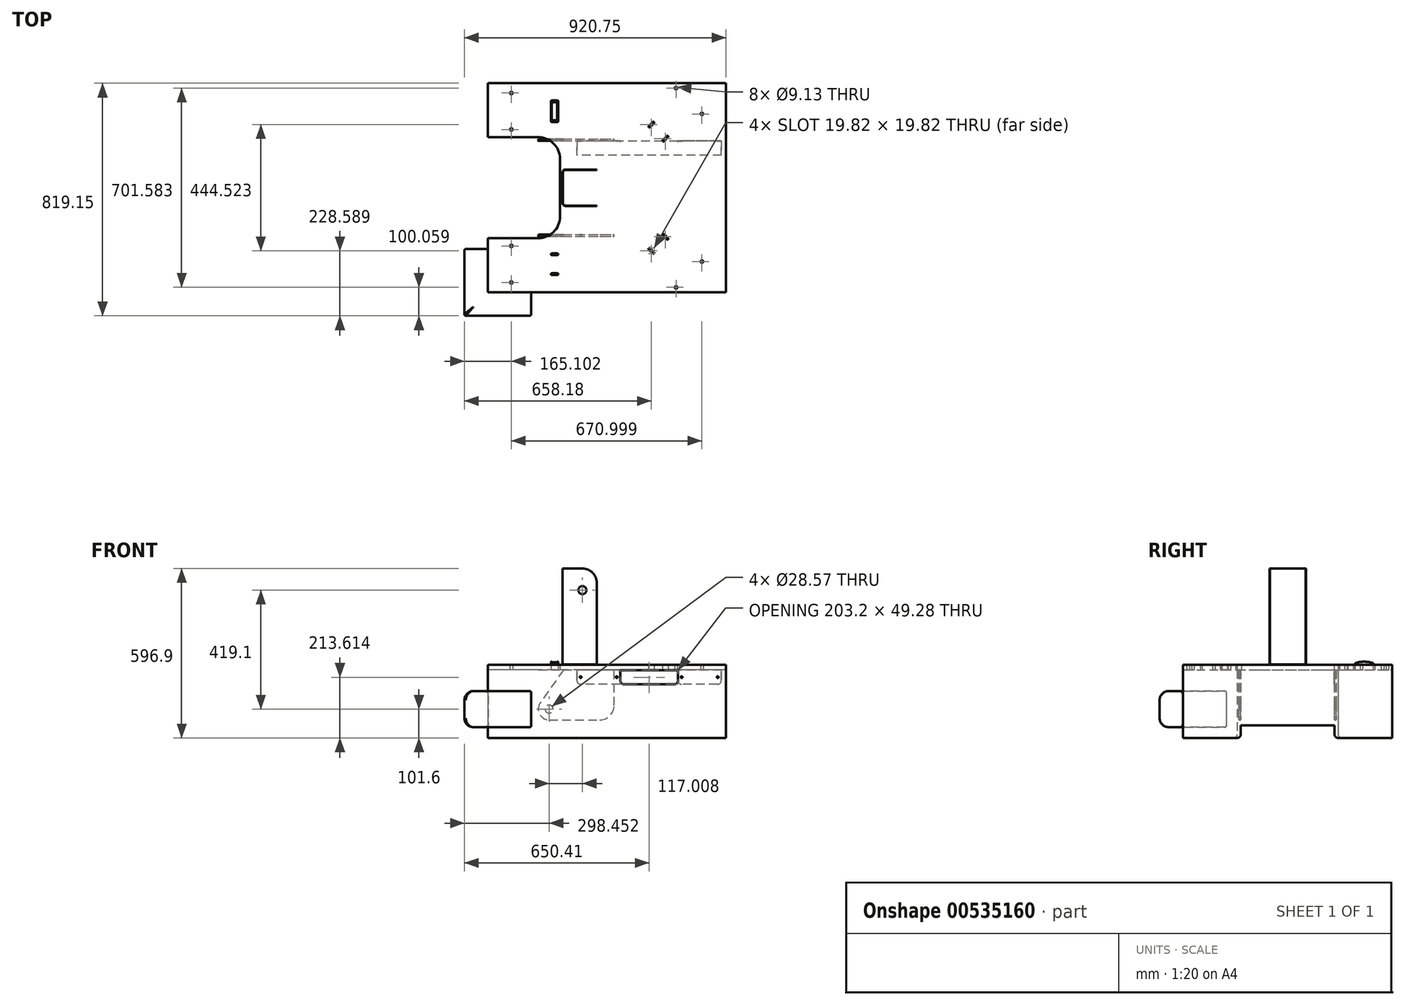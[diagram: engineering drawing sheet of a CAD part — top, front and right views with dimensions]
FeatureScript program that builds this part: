
annotation { "Feature Type Name" : "Feature", "Feature Type Description" : "" }
export const myFeature = defineFeature(function(context is Context, id is Id, definition is map)
    precondition{}
    {
        {
            var Q0;
            Q0=qCreatedBy(makeId("Top.planeOp"),FACE);
            var sketch = newSketch(context, id + "F0", { "sketchPlane" : qUnion([Q0])});
            skLineSegment(sketch, "E0.bottom", {"start": v(-491.66, 457.2) * mm, "end": v(524.34, 457.2) * mm});
            skLineSegment(sketch, "E0.top", {"start": v(-491.66, -457.2) * mm, "end": v(524.34, -457.2) * mm});
            skLineSegment(sketch, "E0.left", {"start": v(-491.66, 457.2) * mm, "end": v(-491.66, -457.2) * mm});
            skLineSegment(sketch, "E0.right", {"start": v(524.34, 457.2) * mm, "end": v(524.34, -457.2) * mm});
            skLineSegment(sketch, "E1.bottom", {"start": v(-301.16, -193.2) * mm, "end": v(-237.66, -193.2) * mm});
            skLineSegment(sketch, "E1.top", {"start": v(-301.16, -345.6) * mm, "end": v(-237.66, -345.6) * mm});
            skLineSegment(sketch, "E1.left", {"start": v(-301.16, -193.2) * mm, "end": v(-301.16, -345.6) * mm});
            skLineSegment(sketch, "E1.right", {"start": v(-237.66, -193.2) * mm, "end": v(-237.66, -345.6) * mm});
            skLineSegment(sketch, "E2.bottom", {"start": v(-301.16, 345.6) * mm, "end": v(-237.66, 345.6) * mm});
            skLineSegment(sketch, "E2.top", {"start": v(-301.16, 193.2) * mm, "end": v(-237.66, 193.2) * mm});
            skLineSegment(sketch, "E2.left", {"start": v(-301.16, 345.6) * mm, "end": v(-301.16, 193.2) * mm});
            skLineSegment(sketch, "E2.right", {"start": v(-237.66, 345.6) * mm, "end": v(-237.66, 193.2) * mm});
            skLineSegment(sketch, "E3", {"start": v(-301.16, -345.6) * mm, "end": v(-237.66, -193.2) * mm, "construction": true});
            skLineSegment(sketch, "E4", {"start": v(-269.4, -269.4) * mm, "end": v(0, 0) * mm, "construction": true});
            skLineSegment(sketch, "E5", {"start": v(-301.16, 345.6) * mm, "end": v(-237.66, 193.2) * mm, "construction": true});
            skLineSegment(sketch, "E6", {"start": v(-269.4, 269.4) * mm, "end": v(0, 0) * mm, "construction": true});
            skLineSegment(sketch, "E7", {"start": v(435.44, -368.3) * mm, "end": v(-402.76, -368.3) * mm, "construction": true});
            skLineSegment(sketch, "E8", {"start": v(-402.76, -368.3) * mm, "end": v(-402.76, 368.3) * mm, "construction": true});
            skLineSegment(sketch, "E9", {"start": v(-402.76, 368.3) * mm, "end": v(435.44, 368.3) * mm, "construction": true});
            skLineSegment(sketch, "E10.bottom", {"start": v(224.5, 332.27) * mm, "end": v(332.27, 224.5) * mm});
            skLineSegment(sketch, "E10.top", {"start": v(206.55, 314.3) * mm, "end": v(314.3, 206.55) * mm});
            skLineSegment(sketch, "E10.left", {"start": v(224.5, 332.27) * mm, "end": v(206.55, 314.3) * mm});
            skLineSegment(sketch, "E10.right", {"start": v(332.27, 224.5) * mm, "end": v(314.3, 206.55) * mm});
            skPoint(sketch, "E10.middle", {"position": v(269.4, 269.4) * mm});
            skLineSegment(sketch, "E11", {"start": v(0, 0) * mm, "end": v(269.4, 269.4) * mm, "construction": true});
            skLineSegment(sketch, "E12.bottom", {"start": v(314.3, -206.55) * mm, "end": v(206.55, -314.3) * mm});
            skLineSegment(sketch, "E12.top", {"start": v(332.27, -224.5) * mm, "end": v(224.5, -332.27) * mm});
            skLineSegment(sketch, "E12.left", {"start": v(314.3, -206.55) * mm, "end": v(332.27, -224.5) * mm});
            skLineSegment(sketch, "E12.right", {"start": v(206.55, -314.3) * mm, "end": v(224.5, -332.27) * mm});
            skPoint(sketch, "E12.middle", {"position": v(269.4, -269.4) * mm});
            skLineSegment(sketch, "E13", {"start": v(0, 0) * mm, "end": v(269.4, -269.4) * mm, "construction": true});
            skLineSegment(sketch, "E14", {"start": v(-402.76, 215.9) * mm, "end": v(-485.3, 215.9) * mm, "construction": true});
            skLineSegment(sketch, "E15", {"start": v(-485.3, 215.9) * mm, "end": v(-485.3, 450.85) * mm, "construction": true});
            skLineSegment(sketch, "E16", {"start": v(-485.3, 450.85) * mm, "end": v(518, 450.85) * mm, "construction": true});
            skLineSegment(sketch, "E17", {"start": v(-402.76, -215.9) * mm, "end": v(-485.3, -215.9) * mm, "construction": true});
            skLineSegment(sketch, "E18", {"start": v(-485.3, -215.9) * mm, "end": v(-485.3, -450.85) * mm, "construction": true});
            skLineSegment(sketch, "E19", {"start": v(-485.3, -450.85) * mm, "end": v(518, -450.85) * mm, "construction": true});
            skCircle(sketch, "E20", {"center": v(-345.42, 0) * mm, "radius": 139.7 * mm, "construction": true});
            skLineSegment(sketch, "E21.bottom", {"start": v(-398.8, 177.8) * mm, "end": v(-170.2, 177.8) * mm, "construction": true});
            skLineSegment(sketch, "E21.top", {"start": v(-398.8, -177.8) * mm, "end": v(-170.2, -177.8) * mm, "construction": true});
            skLineSegment(sketch, "E21.left", {"start": v(-398.8, 177.8) * mm, "end": v(-398.8, -177.8) * mm, "construction": true});
            skLineSegment(sketch, "E21.right", {"start": v(-170.2, 177.8) * mm, "end": v(-170.2, -177.8) * mm, "construction": true});
            skPoint(sketch, "E21.middle", {"position": v(-284.5, 0) * mm});
            skLineSegment(sketch, "E22", {"start": v(-269.4, 269.4) * mm, "end": v(-269.4, 383.7) * mm, "construction": true});
            skLineSegment(sketch, "E23", {"start": v(251.45, 305.33) * mm, "end": v(278.39, 332.27) * mm, "construction": true});
            skLineSegment(sketch, "E24", {"start": v(278.39, 332.27) * mm, "end": v(332.27, 278.39) * mm, "construction": true});
            skLineSegment(sketch, "E25", {"start": v(332.27, 278.39) * mm, "end": v(305.33, 251.45) * mm, "construction": true});
            skPoint(sketch, "E26.startSnap0", {"position": v(260.43, 260.43) * mm});
            skPoint(sketch, "E27", {"position": v(-170.2, 0) * mm});
            skLineSegment(sketch, "E28", {"start": v(435.44, -368.3) * mm, "end": v(435.44, 368.3) * mm, "construction": true});
            skLineSegment(sketch, "E29", {"start": v(518, 450.85) * mm, "end": v(518, -450.85) * mm, "construction": true});
            skSolve(sketch);
        }
        {
            var Q0;
            Q0=qCreatedBy(makeId("Front.planeOp"),FACE);
            var sketch = newSketch(context, id + "F1", { "sketchPlane" : qUnion([Q0])});
            skLineSegment(sketch, "E30.bottom", {"start": v(-491.66, 50.8) * mm, "end": v(-212.26, 50.8) * mm});
            skLineSegment(sketch, "E30.top", {"start": v(-491.66, 0) * mm, "end": v(-212.26, 0) * mm});
            skLineSegment(sketch, "E30.left", {"start": v(-491.66, 50.8) * mm, "end": v(-491.66, 0) * mm});
            skLineSegment(sketch, "E30.right", {"start": v(-212.26, 50.8) * mm, "end": v(-212.26, 0) * mm});
            skCircle(sketch, "E31", {"center": v(-186.86, 114.3) * mm, "radius": 15.32 * mm});
            skLineSegment(sketch, "E32.bottom", {"start": v(-250.36, 139.7) * mm, "end": v(-301.16, 139.7) * mm});
            skLineSegment(sketch, "E32.top", {"start": v(-250.36, 419.1) * mm, "end": v(-301.16, 419.1) * mm});
            skLineSegment(sketch, "E32.left", {"start": v(-250.36, 139.7) * mm, "end": v(-250.36, 419.1) * mm});
            skLineSegment(sketch, "E32.right", {"start": v(-301.16, 139.7) * mm, "end": v(-301.16, 419.1) * mm});
            skLineSegment(sketch, "E33", {"start": v(-491.66, 330.2) * mm, "end": v(-224.96, 330.2) * mm});
            skLineSegment(sketch, "E34", {"start": v(-224.96, 330.2) * mm, "end": v(-263.06, 365.13) * mm});
            skLineSegment(sketch, "E35", {"start": v(-263.06, 365.13) * mm, "end": v(-263.06, 352.43) * mm});
            skLineSegment(sketch, "E36", {"start": v(-263.06, 352.43) * mm, "end": v(-491.66, 352.43) * mm});
            skLineSegment(sketch, "E37", {"start": v(-491.66, 352.43) * mm, "end": v(-491.66, 330.2) * mm});
            skLineSegment(sketch, "E38", {"start": v(-301.16, 364.5) * mm, "end": v(-250.36, 364.5) * mm});
            skArc(sketch, "E39", {"start": v(-186.86, 0) * mm, "mid": v(-106.04, 33.48) * mm, "end": v(-72.56, 114.3) * mm});
            skSolve(sketch);
        }
        {
            var Q0;
            Q0=qCreatedBy(makeId("Top.planeOp"),FACE);
            var sketch = newSketch(context, id + "F2", { "sketchPlane" : qUnion([Q0])});
            skLineSegment(sketch, "E40.0", {"start": v(-402.76, 368.3) * mm, "end": v(435.44, 368.3) * mm});
            skArc(sketch, "E41.0", {"start": v(117.94, -368.3) * mm, "mid": v(486.24, 0) * mm, "end": v(117.94, 368.3) * mm, "construction": true});
            skLineSegment(sketch, "E42.0", {"start": v(435.44, -368.3) * mm, "end": v(-402.76, -368.3) * mm});
            skLineSegment(sketch, "E43.0", {"start": v(-402.76, -368.3) * mm, "end": v(-402.76, 368.3) * mm});
            skLineSegment(sketch, "E44.0", {"start": v(117.94, 368.3) * mm, "end": v(245.94, 368.3) * mm, "construction": true});
            skArc(sketch, "E45.0", {"start": v(283.93, 367.12) * mm, "mid": v(264.94, 368) * mm, "end": v(245.94, 368.3) * mm, "construction": true});
            skArc(sketch, "E46.0", {"start": v(283.93, 367.12) * mm, "mid": v(323.68, 354.89) * mm, "end": v(353.52, 325.92) * mm, "construction": true});
            skArc(sketch, "E47.0", {"start": v(353.52, 325.92) * mm, "mid": v(447.96, 0) * mm, "end": v(353.52, -325.92) * mm, "construction": true});
            skArc(sketch, "E48.0", {"start": v(353.52, -325.92) * mm, "mid": v(323.68, -354.89) * mm, "end": v(283.93, -367.12) * mm, "construction": true});
            skArc(sketch, "E49.0", {"start": v(283.93, -367.12) * mm, "mid": v(264.94, -368) * mm, "end": v(245.94, -368.3) * mm, "construction": true});
            skLineSegment(sketch, "E50.0", {"start": v(117.94, -368.3) * mm, "end": v(245.94, -368.3) * mm, "construction": true});
            skLineSegment(sketch, "E51.0", {"start": v(435.44, -368.3) * mm, "end": v(435.44, 368.3) * mm});
            skSolve(sketch);
        }
        {
            var Q0;
            Q0=qSketchRegion(id+"F2",true);
            extrude(context, id + "F3", {"entities" : qUnion([Q0]), "depth" : 254 * mm, "hasSecondDirection" : true, "secondDirectionOppositeDirection" : true, "secondDirectionDepth" : -12.7 * mm});
        }
        {
            var Q0;
            Q0=makeQuery(id+"F3.opExtrude","CAP_FACE",FACE,{"disambiguationData":[OSD([sQuery(id+"F2.wireOp",EDGE,"E40.0"),sQuery(id+"F2.wireOp",EDGE,"E41.0"),sQuery(id+"F2.wireOp",EDGE,"E42.0"),sQuery(id+"F2.wireOp",EDGE,"E43.0")])],"isStart":true});
            shell(context, id + "F4", {"entities" : qUnion([Q0]), "thickness" : 1.52 * mm});
        }
        {
            var Q0;
            Q0=qCreatedBy(makeId("Top.planeOp"),FACE);
            var sketch = newSketch(context, id + "F5", { "sketchPlane" : qUnion([Q0])});
            skLineSegment(sketch, "E52.bottom", {"start": v(-402.76, 177.8) * mm, "end": v(-148.76, 177.8) * mm});
            skLineSegment(sketch, "E52.top", {"start": v(-402.76, -177.8) * mm, "end": v(-148.76, -177.8) * mm});
            skLineSegment(sketch, "E52.left", {"start": v(-402.76, 177.8) * mm, "end": v(-402.76, -177.8) * mm});
            skLineSegment(sketch, "E52.right", {"start": v(-148.76, 177.8) * mm, "end": v(-148.76, -177.8) * mm});
            skSolve(sketch);
        }
        {
            var Q0;
            Q0=qSketchRegion(id+"F5",true);
            extrude(context, id + "F6", {"entities" : qUnion([Q0]), "operationType" : NewBodyOperationType.REMOVE, "endBound" : BoundingType.THROUGH_ALL, "depth" : 25.4 * mm});
        }
        {
            var Q0;
            Q0=makeQuery(id+"F6.boolean.opBoolean","COPY",EDGE,{"derivedFrom":makeQuery(id+"F6.opExtrude","SWEPT_EDGE",EDGE,{"disambiguationData":[OSD([sQuery(id+"F5.wireOp",EDGE,"E52.bottom"),sQuery(id+"F5.wireOp",EDGE,"E52.right")])]})});
            var Q1;
            Q1=makeQuery(id+"F6.boolean.opBoolean","COPY",EDGE,{"derivedFrom":makeQuery(id+"F6.opExtrude","SWEPT_EDGE",EDGE,{"disambiguationData":[OSD([sQuery(id+"F5.wireOp",EDGE,"E52.top"),sQuery(id+"F5.wireOp",EDGE,"E52.right")])]})});
            fillet(context, id + "F7", {"entities" : qUnion([Q0, Q1]), "radius" : 76.2 * mm, "tangentPropagation" : true, "allowEdgeOverflow" : false});
        }
        {
            var Q0;
            Q0=makeQuery(id+"F6.boolean.opBoolean","INTERSECT",EDGE,{"derivedFrom":[makeQuery(id+"F3.opExtrude","CAP_FACE",FACE,{"disambiguationData":[OSD([sQuery(id+"F2.wireOp",EDGE,"E40.0"),sQuery(id+"F2.wireOp",EDGE,"E41.0"),sQuery(id+"F2.wireOp",EDGE,"E42.0"),sQuery(id+"F2.wireOp",EDGE,"E43.0")])],"isStart":true}),makeQuery(id+"F6.opExtrude","SWEPT_FACE",FACE,{"disambiguationData":[OSD([sQuery(id+"F5.wireOp",EDGE,"E52.bottom")])]})]});
            var Q1;
            Q1=makeQuery(id+"F6.boolean.opBoolean","INTERSECT",EDGE,{"derivedFrom":[makeQuery(id+"F3.opExtrude","CAP_FACE",FACE,{"disambiguationData":[OSD([sQuery(id+"F2.wireOp",EDGE,"E40.0"),sQuery(id+"F2.wireOp",EDGE,"E41.0"),sQuery(id+"F2.wireOp",EDGE,"E42.0"),sQuery(id+"F2.wireOp",EDGE,"E43.0")])],"isStart":true}),makeQuery(id+"F6.opExtrude","SWEPT_FACE",FACE,{"disambiguationData":[OSD([sQuery(id+"F5.wireOp",EDGE,"E52.top")])]})]});
            fillet(context, id + "F8", {"entities" : qUnion([Q0, Q1]), "radius" : 12.7 * mm, "tangentPropagation" : true, "allowEdgeOverflow" : false});
        }
        {
            var Q0;
            Q0=qCreatedBy(makeId("Top.planeOp"),FACE);
            var sketch = newSketch(context, id + "F9", { "sketchPlane" : qUnion([Q0])});
            skLineSegment(sketch, "E53.0", {"start": v(-402.76, 215.9) * mm, "end": v(-485.3, 215.9) * mm});
            skLineSegment(sketch, "E54.0", {"start": v(-485.3, 215.9) * mm, "end": v(-485.3, 450.85) * mm});
            skLineSegment(sketch, "E55.0", {"start": v(-485.3, 450.85) * mm, "end": v(518, 450.85) * mm});
            skLineSegment(sketch, "E56.0", {"start": v(-485.3, -450.85) * mm, "end": v(518, -450.85) * mm});
            skLineSegment(sketch, "E57.0", {"start": v(-485.3, -215.9) * mm, "end": v(-485.3, -450.85) * mm});
            skLineSegment(sketch, "E58.0", {"start": v(-402.76, -215.9) * mm, "end": v(-485.3, -215.9) * mm});
            skLineSegment(sketch, "E59.0", {"start": v(435.44, -368.3) * mm, "end": v(-402.76, -368.3) * mm});
            skLineSegment(sketch, "E60.0", {"start": v(-402.76, 368.3) * mm, "end": v(435.44, 368.3) * mm});
            skLineSegment(sketch, "E61.0", {"start": v(-402.76, -368.3) * mm, "end": v(-402.76, 368.3) * mm});
            skLineSegment(sketch, "E62", {"start": v(-402.76, 215.9) * mm, "end": v(-402.76, 368.3) * mm});
            skLineSegment(sketch, "E63", {"start": v(-402.76, -215.9) * mm, "end": v(-402.76, -368.3) * mm});
            skLineSegment(sketch, "E64.0", {"start": v(518, 450.85) * mm, "end": v(518, -450.85) * mm});
            skLineSegment(sketch, "E65", {"start": v(-250.36, 368.3) * mm, "end": v(-250.36, 450.85) * mm});
            skLineSegment(sketch, "E66", {"start": v(-250.36, -368.3) * mm, "end": v(-250.36, -450.85) * mm});
            skLineSegment(sketch, "E67", {"start": v(283.04, 450.85) * mm, "end": v(283.04, 368.3) * mm});
            skLineSegment(sketch, "E68", {"start": v(283.04, -368.3) * mm, "end": v(283.04, -450.85) * mm});
            skLineSegment(sketch, "E69", {"start": v(518, 215.9) * mm, "end": v(435.44, 215.9) * mm});
            skLineSegment(sketch, "E70.0", {"start": v(435.44, -368.3) * mm, "end": v(435.44, 368.3) * mm});
            skLineSegment(sketch, "E71", {"start": v(435.44, -215.9) * mm, "end": v(518, -215.9) * mm});
            skSolve(sketch);
        }
        {
            var Q0;
            {var subQ3=sQuery(id+"F9.wireOp",EDGE,"E57.0");Q0=makeQuery(id+"F9.imprint","IMPRINT",FACE,{"disambiguationData":[TD([[makeQuery(id+"F9.imprint","IMPRINT",EDGE,{"derivedFrom":subQ3}),1.0]])]});}
            extrude(context, id + "F10", {"entities" : qUnion([Q0]), "depth" : 177.8 * mm, "hasSecondDirection" : true, "secondDirectionOppositeDirection" : true, "secondDirectionDepth" : -50.8 * mm, "offsetDistance" : 25.4 * mm});
        }
        {
            var Q0;
            Q0=makeQuery(id+"F10.opExtrude","CAP_EDGE",EDGE,{"disambiguationData":[OSD([sQuery(id+"F9.wireOp",EDGE,"E57.0")])],"isStart":false});
            var Q1;
            Q1=makeQuery(id+"F10.opExtrude","CAP_EDGE",EDGE,{"disambiguationData":[OSD([sQuery(id+"F9.wireOp",EDGE,"E56.0")])],"isStart":false});
            var Q2;
            Q2=makeQuery(id+"F10.opExtrude","CAP_EDGE",EDGE,{"disambiguationData":[OSD([sQuery(id+"F9.wireOp",EDGE,"E54.0")])],"isStart":false});
            var Q3;
            Q3=makeQuery(id+"F10.opExtrude","CAP_EDGE",EDGE,{"disambiguationData":[OSD([sQuery(id+"F9.wireOp",EDGE,"E56.0")])],"isStart":true});
            var Q4;
            Q4=makeQuery(id+"F10.opExtrude","CAP_EDGE",EDGE,{"disambiguationData":[OSD([sQuery(id+"F9.wireOp",EDGE,"E57.0")])],"isStart":true});
            var Q5;
            Q5=makeQuery(id+"F10.opExtrude","CAP_EDGE",EDGE,{"disambiguationData":[OSD([sQuery(id+"F9.wireOp",EDGE,"E54.0")])],"isStart":true});
            var Q6;
            {var subQ0=sQuery(id+"F9.wireOp",EDGE,"E55.0");Q6=makeQuery(id+"F10.opExtrude","CAP_EDGE",EDGE,{"disambiguationData":[OSD([subQ0]),TDD([makeQuery(id+"F9.imprint","IMPRINT",EDGE,{"disambiguationData":[TD([[makeQuery(id+"F9.imprint","INTERSECT",VERTEX,{"derivedFrom":[sQuery(id+"F9.wireOp",EDGE,"E54.0"),subQ0]}),-1.0]])],"derivedFrom":subQ0})])],"isStart":false});}
            var Q7;
            {var subQ0=sQuery(id+"F9.wireOp",EDGE,"E55.0");Q7=makeQuery(id+"F10.opExtrude","CAP_EDGE",EDGE,{"disambiguationData":[OSD([subQ0]),TDD([makeQuery(id+"F9.imprint","IMPRINT",EDGE,{"disambiguationData":[TD([[makeQuery(id+"F9.imprint","INTERSECT",VERTEX,{"derivedFrom":[sQuery(id+"F9.wireOp",EDGE,"E54.0"),subQ0]}),-1.0]])],"derivedFrom":subQ0})])],"isStart":true});}
            var Q8;
            {var subQ0=sQuery(id+"F9.wireOp",EDGE,"E55.0");Q8=makeQuery(id+"F10.opExtrude","CAP_EDGE",EDGE,{"disambiguationData":[OSD([subQ0]),TDD([makeQuery(id+"F9.imprint","IMPRINT",EDGE,{"disambiguationData":[TD([[makeQuery(id+"F9.imprint","INTERSECT",VERTEX,{"derivedFrom":[subQ0,sQuery(id+"F9.wireOp",EDGE,"E64.0")]}),1.0]])],"derivedFrom":subQ0})])],"isStart":true});}
            var Q9;
            {var subQ0=sQuery(id+"F9.wireOp",EDGE,"E55.0");Q9=makeQuery(id+"F10.opExtrude","CAP_EDGE",EDGE,{"disambiguationData":[OSD([subQ0]),TDD([makeQuery(id+"F9.imprint","IMPRINT",EDGE,{"disambiguationData":[TD([[makeQuery(id+"F9.imprint","INTERSECT",VERTEX,{"derivedFrom":[subQ0,sQuery(id+"F9.wireOp",EDGE,"E64.0")]}),1.0]])],"derivedFrom":subQ0})])],"isStart":false});}
            var Q10;
            {var subQ0=sQuery(id+"F9.wireOp",EDGE,"E64.0");Q10=makeQuery(id+"F10.opExtrude","CAP_EDGE",EDGE,{"disambiguationData":[OSD([subQ0]),TDD([makeQuery(id+"F9.imprint","IMPRINT",EDGE,{"disambiguationData":[TD([[makeQuery(id+"F9.imprint","INTERSECT",VERTEX,{"derivedFrom":[sQuery(id+"F9.wireOp",EDGE,"E55.0"),subQ0]}),-1.0]])],"derivedFrom":subQ0})])],"isStart":true});}
            var Q11;
            {var subQ0=sQuery(id+"F9.wireOp",EDGE,"E64.0");Q11=makeQuery(id+"F10.opExtrude","CAP_EDGE",EDGE,{"disambiguationData":[OSD([subQ0]),TDD([makeQuery(id+"F9.imprint","IMPRINT",EDGE,{"disambiguationData":[TD([[makeQuery(id+"F9.imprint","INTERSECT",VERTEX,{"derivedFrom":[sQuery(id+"F9.wireOp",EDGE,"E55.0"),subQ0]}),-1.0]])],"derivedFrom":subQ0})])],"isStart":false});}
            var Q12;
            {var subQ0=sQuery(id+"F9.wireOp",EDGE,"E64.0");Q12=makeQuery(id+"F10.opExtrude","CAP_EDGE",EDGE,{"disambiguationData":[OSD([subQ0]),TDD([makeQuery(id+"F9.imprint","IMPRINT",EDGE,{"disambiguationData":[TD([[makeQuery(id+"F9.imprint","INTERSECT",VERTEX,{"derivedFrom":[sQuery(id+"F9.wireOp",EDGE,"E56.0"),subQ0]}),1.0]])],"derivedFrom":subQ0})])],"isStart":true});}
            var Q13;
            {var subQ0=sQuery(id+"F9.wireOp",EDGE,"E64.0");Q13=makeQuery(id+"F10.opExtrude","CAP_EDGE",EDGE,{"disambiguationData":[OSD([subQ0]),TDD([makeQuery(id+"F9.imprint","IMPRINT",EDGE,{"disambiguationData":[TD([[makeQuery(id+"F9.imprint","INTERSECT",VERTEX,{"derivedFrom":[sQuery(id+"F9.wireOp",EDGE,"E56.0"),subQ0]}),1.0]])],"derivedFrom":subQ0})])],"isStart":false});}
            fillet(context, id + "F11", {"entities" : qUnion([Q0, Q1, Q2, Q3, Q4, Q5, Q6, Q7, Q8, Q9, Q10, Q11, Q12, Q13]), "radius" : 31.75 * mm, "tangentPropagation" : true, "allowEdgeOverflow" : false});
        }
        {
            var Q0;
            Q0=makeQuery(id+"F10.opExtrude","SWEPT_EDGE",EDGE,{"disambiguationData":[OSD([sQuery(id+"F9.wireOp",EDGE,"E53.0"),sQuery(id+"F9.wireOp",EDGE,"E54.0")])]});
            var Q1;
            Q1=makeQuery(id+"F10.opExtrude","SWEPT_EDGE",EDGE,{"disambiguationData":[OSD([sQuery(id+"F9.wireOp",EDGE,"E57.0"),sQuery(id+"F9.wireOp",EDGE,"E58.0")])]});
            var Q2;
            Q2=makeQuery(id+"F10.opExtrude","SWEPT_EDGE",EDGE,{"disambiguationData":[OSD([sQuery(id+"F9.wireOp",EDGE,"E53.0"),sQuery(id+"F9.wireOp",EDGE,"E61.0"),sQuery(id+"F9.wireOp",EDGE,"E62")])]});
            var Q3;
            Q3=makeQuery(id+"F11.opFillet","BLEND_EDGE",EDGE,{"blendedFrom":[makeQuery(id+"F10.opExtrude","CAP_EDGE",EDGE,{"disambiguationData":[OSD([sQuery(id+"F9.wireOp",EDGE,"E56.0")])],"isStart":false}),makeQuery(id+"F10.opExtrude","CAP_EDGE",EDGE,{"disambiguationData":[OSD([sQuery(id+"F9.wireOp",EDGE,"E57.0")])],"isStart":false})],"blendedInto":[]});
            var Q4;
            Q4=makeQuery(id+"F11.opFillet","BLEND_EDGE",EDGE,{"blendedFrom":[makeQuery(id+"F10.opExtrude","CAP_EDGE",EDGE,{"disambiguationData":[OSD([sQuery(id+"F9.wireOp",EDGE,"E54.0")])],"isStart":false}),makeQuery(id+"F10.opExtrude","CAP_EDGE",EDGE,{"disambiguationData":[OSD([sQuery(id+"F9.wireOp",EDGE,"E55.0")])],"isStart":false})],"blendedInto":[]});
            var Q5;
            Q5=makeQuery(id+"F10.opExtrude","SWEPT_EDGE",EDGE,{"disambiguationData":[OSD([sQuery(id+"F9.wireOp",EDGE,"E58.0"),sQuery(id+"F9.wireOp",EDGE,"E61.0"),sQuery(id+"F9.wireOp",EDGE,"E63")])]});
            var Q6;
            Q6=makeQuery(id+"F10.opExtrude","SWEPT_EDGE",EDGE,{"disambiguationData":[OSD([sQuery(id+"F9.wireOp",EDGE,"E55.0"),sQuery(id+"F9.wireOp",EDGE,"E65")])]});
            var Q7;
            Q7=makeQuery(id+"F10.opExtrude","SWEPT_EDGE",EDGE,{"disambiguationData":[OSD([sQuery(id+"F9.wireOp",EDGE,"E60.0"),sQuery(id+"F9.wireOp",EDGE,"E65")])]});
            var Q8;
            Q8=makeQuery(id+"F10.opExtrude","SWEPT_EDGE",EDGE,{"disambiguationData":[OSD([sQuery(id+"F9.wireOp",EDGE,"E55.0"),sQuery(id+"F9.wireOp",EDGE,"E67")])]});
            var Q9;
            Q9=makeQuery(id+"F10.opExtrude","SWEPT_EDGE",EDGE,{"disambiguationData":[OSD([sQuery(id+"F9.wireOp",EDGE,"E60.0"),sQuery(id+"F9.wireOp",EDGE,"E67")])]});
            var Q10;
            Q10=makeQuery(id+"F10.opExtrude","SWEPT_EDGE",EDGE,{"disambiguationData":[OSD([sQuery(id+"F9.wireOp",EDGE,"E55.0"),sQuery(id+"F9.wireOp",EDGE,"E64.0")])]});
            var Q11;
            Q11=makeQuery(id+"F10.opExtrude","SWEPT_EDGE",EDGE,{"disambiguationData":[OSD([sQuery(id+"F9.wireOp",EDGE,"E64.0"),sQuery(id+"F9.wireOp",EDGE,"E69")])]});
            var Q12;
            Q12=makeQuery(id+"F10.opExtrude","SWEPT_EDGE",EDGE,{"disambiguationData":[OSD([sQuery(id+"F9.wireOp",EDGE,"E69"),sQuery(id+"F9.wireOp",EDGE,"E70.0")])]});
            var Q13;
            Q13=makeQuery(id+"F10.opExtrude","SWEPT_EDGE",EDGE,{"disambiguationData":[OSD([sQuery(id+"F9.wireOp",EDGE,"E64.0"),sQuery(id+"F9.wireOp",EDGE,"E71")])]});
            var Q14;
            Q14=makeQuery(id+"F10.opExtrude","SWEPT_EDGE",EDGE,{"disambiguationData":[OSD([sQuery(id+"F9.wireOp",EDGE,"E70.0"),sQuery(id+"F9.wireOp",EDGE,"E71")])]});
            var Q15;
            Q15=makeQuery(id+"F10.opExtrude","SWEPT_EDGE",EDGE,{"disambiguationData":[OSD([sQuery(id+"F9.wireOp",EDGE,"E56.0"),sQuery(id+"F9.wireOp",EDGE,"E64.0")])]});
            var Q16;
            Q16=makeQuery(id+"F10.opExtrude","SWEPT_EDGE",EDGE,{"disambiguationData":[OSD([sQuery(id+"F9.wireOp",EDGE,"E56.0"),sQuery(id+"F9.wireOp",EDGE,"E68")])]});
            var Q17;
            Q17=makeQuery(id+"F10.opExtrude","SWEPT_EDGE",EDGE,{"disambiguationData":[OSD([sQuery(id+"F9.wireOp",EDGE,"E59.0"),sQuery(id+"F9.wireOp",EDGE,"E68")])]});
            var Q18;
            Q18=makeQuery(id+"F10.opExtrude","SWEPT_EDGE",EDGE,{"disambiguationData":[OSD([sQuery(id+"F9.wireOp",EDGE,"E56.0"),sQuery(id+"F9.wireOp",EDGE,"E66")])]});
            var Q19;
            Q19=makeQuery(id+"F10.opExtrude","SWEPT_EDGE",EDGE,{"disambiguationData":[OSD([sQuery(id+"F9.wireOp",EDGE,"E59.0"),sQuery(id+"F9.wireOp",EDGE,"E66")])]});
            fillet(context, id + "F12", {"entities" : qUnion([Q0, Q1, Q2, Q3, Q4, Q5, Q6, Q7, Q8, Q9, Q10, Q11, Q12, Q13, Q14, Q15, Q16, Q17, Q18, Q19]), "radius" : 5.08 * mm, "tangentPropagation" : true, "allowEdgeOverflow" : false});
        }
        {
            var Q0;
            Q0=qCreatedBy(makeId("Front.planeOp"),FACE);
            var sketch = newSketch(context, id + "F13", { "sketchPlane" : qUnion([Q0])});
            skLineSegment(sketch, "E72", {"start": v(-136.62, 252.48) * mm, "end": v(-218.07, 136.15) * mm});
            skLineSegment(sketch, "E73", {"start": v(-136.62, 252.48) * mm, "end": v(41.74, 252.48) * mm});
            skArc(sketch, "E74", {"start": v(-186.86, 76.2) * mm, "mid": v(-220.65, 96.7) * mm, "end": v(-218.07, 136.15) * mm});
            skCircle(sketch, "E75", {"center": v(-186.86, 114.3) * mm, "radius": 14.29 * mm});
            skLineSegment(sketch, "E76", {"start": v(-186.86, 76.2) * mm, "end": v(41.74, 76.2) * mm});
            skLineSegment(sketch, "E77", {"start": v(41.74, 76.2) * mm, "end": v(41.74, 252.48) * mm});
            skCircle(sketch, "E78", {"center": v(-147.23, 150.11) * mm, "radius": 3.18 * mm});
            skSolve(sketch);
        }
        {
            var Q0;
            Q0=makeQuery(id+"F13.imprint","IMPRINT",FACE,{"disambiguationData":[TD([[makeQuery(id+"F13.imprint","IMPRINT",EDGE,{"derivedFrom":sQuery(id+"F13.wireOp",EDGE,"E72")}),1.0]])]});
            extrude(context, id + "F14", {"entities" : qUnion([Q0]), "operationType" : NewBodyOperationType.ADD, "endBound" : BoundingType.SYMMETRIC, "depth" : 342.9 * mm, "offsetDistance" : 25.4 * mm});
        }
        {
            var Q0;
            Q0=qSketchRegion(id+"F13",true);
            extrude(context, id + "F15", {"entities" : qUnion([Q0]), "operationType" : NewBodyOperationType.REMOVE, "endBound" : BoundingType.SYMMETRIC, "oppositeDirection" : true, "depth" : 330.2 * mm, "offsetDistance" : 25.4 * mm});
        }
        {
            var Q0;
            {var subQ0=sQuery(id+"F13.wireOp",EDGE,"E77");var subQ1=sQuery(id+"F13.wireOp",EDGE,"E76");var subQ2=sQuery(id+"F13.wireOp",EDGE,"E75");var subQ3=sQuery(id+"F13.wireOp",EDGE,"E74");var subQ4=sQuery(id+"F13.wireOp",EDGE,"E73");var subQ5=sQuery(id+"F13.wireOp",EDGE,"E72");Q0=makeQuery(id+"F15.boolean.opBoolean","SPLIT",EDGE,{"disambiguationData":[TD([makeQuery(id+"F14.opExtrude","CAP_FACE",FACE,{"disambiguationData":[OSD([subQ5,subQ4,subQ3,subQ2,subQ1,subQ0])],"isStart":false})])],"derivedFrom":makeQuery(id+"F14.opExtrude","SWEPT_EDGE",EDGE,{"disambiguationData":[OSD([subQ1,subQ0])]})});}
            var Q1;
            {var subQ0=sQuery(id+"F13.wireOp",EDGE,"E77");var subQ1=sQuery(id+"F13.wireOp",EDGE,"E76");var subQ2=sQuery(id+"F13.wireOp",EDGE,"E75");var subQ3=sQuery(id+"F13.wireOp",EDGE,"E74");var subQ4=sQuery(id+"F13.wireOp",EDGE,"E73");var subQ5=sQuery(id+"F13.wireOp",EDGE,"E72");Q1=makeQuery(id+"F15.boolean.opBoolean","SPLIT",EDGE,{"disambiguationData":[TD([makeQuery(id+"F14.opExtrude","CAP_FACE",FACE,{"disambiguationData":[OSD([subQ5,subQ4,subQ3,subQ2,subQ1,subQ0])],"isStart":true})])],"derivedFrom":makeQuery(id+"F14.opExtrude","SWEPT_EDGE",EDGE,{"disambiguationData":[OSD([subQ1,subQ0])]})});}
            fillet(context, id + "F16", {"entities" : qUnion([Q0, Q1]), "radius" : 50.8 * mm, "tangentPropagation" : true, "allowEdgeOverflow" : false});
        }
        {
            var Q0;
            Q0=qCreatedBy(makeId("Right.planeOp"),FACE);
            var sketch = newSketch(context, id + "F17", { "sketchPlane" : qUnion([Q0])});
            skLineSegment(sketch, "E79.bottom", {"start": v(64.26, 609.6) * mm, "end": v(-64.26, 609.6) * mm});
            skLineSegment(sketch, "E79.top", {"start": v(64.26, 271.4) * mm, "end": v(-64.26, 271.4) * mm});
            skLineSegment(sketch, "E79.left", {"start": v(64.26, 609.6) * mm, "end": v(64.26, 271.4) * mm});
            skLineSegment(sketch, "E79.right", {"start": v(-64.26, 609.6) * mm, "end": v(-64.26, 271.4) * mm});
            skSolve(sketch);
        }
        {
            var Q0;
            Q0=makeQuery(id+"F17.imprint","IMPRINT",FACE,{"disambiguationData":[TD([[makeQuery(id+"F17.imprint","IMPRINT",EDGE,{"derivedFrom":sQuery(id+"F17.wireOp",EDGE,"E79.bottom")}),1.0]])]});
            extrude(context, id + "F18", {"entities" : qUnion([Q0]), "oppositeDirection" : true, "depth" : 139.7 * mm, "hasSecondDirection" : true, "secondDirectionOppositeDirection" : false, "secondDirectionDepth" : -19.05 * mm, "offsetDistance" : 25.4 * mm});
        }
        {
            var Q0;
            Q0=makeQuery(id+"F3.opExtrude","CAP_FACE",FACE,{"disambiguationData":[OSD([sQuery(id+"F2.wireOp",EDGE,"E40.0"),sQuery(id+"F2.wireOp",EDGE,"E42.0"),sQuery(id+"F2.wireOp",EDGE,"E43.0"),sQuery(id+"F2.wireOp",EDGE,"E44.0"),sQuery(id+"F2.wireOp",EDGE,"E45.0"),sQuery(id+"F2.wireOp",EDGE,"E46.0"),sQuery(id+"F2.wireOp",EDGE,"E47.0"),sQuery(id+"F2.wireOp",EDGE,"E48.0"),sQuery(id+"F2.wireOp",EDGE,"E49.0"),sQuery(id+"F2.wireOp",EDGE,"E50.0")])],"isStart":false});
            extrude(context, id + "F19", {"entities" : qUnion([Q0]), "operationType" : NewBodyOperationType.ADD, "depth" : 15.88 * mm, "offsetDistance" : 25.4 * mm});
        }
        {
            var Q0;
            Q0=qCreatedBy(makeId("Top.planeOp"),FACE);
            var sketch = newSketch(context, id + "F20", { "sketchPlane" : qUnion([Q0])});
            skLineSegment(sketch, "E80", {"start": v(-269.4, 269.4) * mm, "end": v(-320.2, 269.4) * mm, "construction": true});
            skLineSegment(sketch, "E81", {"start": v(-320.2, 205.11) * mm, "end": v(-320.2, 333.7) * mm, "construction": true});
            skCircle(sketch, "E82", {"center": v(-320.2, 205.11) * mm, "radius": 4.56 * mm});
            skCircle(sketch, "E83", {"center": v(-320.2, 333.7) * mm, "radius": 4.56 * mm});
            skCircle(sketch, "E84", {"center": v(-320.2, -205.11) * mm, "radius": 4.56 * mm});
            skCircle(sketch, "E85", {"center": v(-320.2, -333.7) * mm, "radius": 4.56 * mm});
            skCircle(sketch, "E86", {"center": v(259.87, 350.8) * mm, "radius": 4.56 * mm});
            skCircle(sketch, "E87", {"center": v(350.8, 259.87) * mm, "radius": 4.56 * mm});
            skCircle(sketch, "E88", {"center": v(350.8, -259.87) * mm, "radius": 4.56 * mm});
            skCircle(sketch, "E89", {"center": v(259.87, -350.8) * mm, "radius": 4.56 * mm});
            skLineSegment(sketch, "E90", {"start": v(259.87, 350.8) * mm, "end": v(350.8, 259.87) * mm, "construction": true});
            skLineSegment(sketch, "E91", {"start": v(305.33, 305.33) * mm, "end": v(269.4, 269.4) * mm, "construction": true});
            skLineSegment(sketch, "E92", {"start": v(-177.33, 307.5) * mm, "end": v(-158.28, 307.5) * mm});
            skLineSegment(sketch, "E93", {"start": v(-177.33, 301.16) * mm, "end": v(-158.28, 301.16) * mm});
            skArc(sketch, "E94", {"start": v(-177.33, 307.5) * mm, "mid": v(-180.5, 304.33) * mm, "end": v(-177.33, 301.16) * mm});
            skArc(sketch, "E95", {"start": v(-158.28, 301.16) * mm, "mid": v(-155.1, 304.33) * mm, "end": v(-158.28, 307.5) * mm});
            skLineSegment(sketch, "E96.MirrorCS", {"start": v(-177.33, 237.66) * mm, "end": v(-158.28, 237.66) * mm});
            skArc(sketch, "E97.MirrorCS", {"start": v(-177.33, 231.3) * mm, "mid": v(-180.5, 234.48) * mm, "end": v(-177.33, 237.66) * mm});
            skLineSegment(sketch, "E98.MirrorCS", {"start": v(-177.33, 231.3) * mm, "end": v(-158.28, 231.3) * mm});
            skArc(sketch, "E99.MirrorCS", {"start": v(-158.28, 237.66) * mm, "mid": v(-155.1, 234.48) * mm, "end": v(-158.28, 231.3) * mm});
            skLineSegment(sketch, "E100", {"start": v(181.85, 226.75) * mm, "end": v(168.38, 213.28) * mm});
            skLineSegment(sketch, "E101", {"start": v(177.36, 231.24) * mm, "end": v(163.89, 217.77) * mm});
            skArc(sketch, "E102", {"start": v(163.89, 217.77) * mm, "mid": v(163.89, 213.28) * mm, "end": v(168.38, 213.28) * mm});
            skArc(sketch, "E103", {"start": v(177.36, 231.24) * mm, "mid": v(181.85, 231.24) * mm, "end": v(181.85, 226.75) * mm});
            skArc(sketch, "E104.MirrorCS", {"start": v(231.24, 177.36) * mm, "mid": v(231.24, 181.85) * mm, "end": v(226.75, 181.85) * mm});
            skArc(sketch, "E105.MirrorCS", {"start": v(217.77, 163.89) * mm, "mid": v(213.28, 163.89) * mm, "end": v(213.28, 168.38) * mm});
            skLineSegment(sketch, "E106.MirrorCS", {"start": v(231.24, 177.36) * mm, "end": v(217.77, 163.89) * mm});
            skLineSegment(sketch, "E107.MirrorCS", {"start": v(226.75, 181.85) * mm, "end": v(213.28, 168.38) * mm});
            skArc(sketch, "E108.MirrorCS", {"start": v(217.77, -163.89) * mm, "mid": v(213.28, -163.89) * mm, "end": v(213.28, -168.38) * mm});
            skArc(sketch, "E109.MirrorCS", {"start": v(231.24, -177.36) * mm, "mid": v(231.24, -181.85) * mm, "end": v(226.75, -181.85) * mm});
            skArc(sketch, "E110.MirrorCS", {"start": v(163.89, -217.77) * mm, "mid": v(163.89, -213.28) * mm, "end": v(168.38, -213.28) * mm});
            skArc(sketch, "E111.MirrorCS", {"start": v(177.36, -231.24) * mm, "mid": v(181.85, -231.24) * mm, "end": v(181.85, -226.75) * mm});
            skLineSegment(sketch, "E112.MirrorCS", {"start": v(231.24, -177.36) * mm, "end": v(217.77, -163.89) * mm});
            skLineSegment(sketch, "E113.MirrorCS", {"start": v(177.36, -231.24) * mm, "end": v(163.89, -217.77) * mm});
            skLineSegment(sketch, "E114.MirrorCS", {"start": v(226.75, -181.85) * mm, "end": v(213.28, -168.38) * mm});
            skLineSegment(sketch, "E115.MirrorCS", {"start": v(181.85, -226.75) * mm, "end": v(168.38, -213.28) * mm});
            skArc(sketch, "E116.MirrorCS", {"start": v(-158.28, -237.66) * mm, "mid": v(-155.1, -234.48) * mm, "end": v(-158.28, -231.3) * mm});
            skArc(sketch, "E117.MirrorCS", {"start": v(-158.28, -301.16) * mm, "mid": v(-155.1, -304.33) * mm, "end": v(-158.28, -307.5) * mm});
            skArc(sketch, "E118.MirrorCS", {"start": v(-177.33, -307.5) * mm, "mid": v(-180.5, -304.33) * mm, "end": v(-177.33, -301.16) * mm});
            skArc(sketch, "E119.MirrorCS", {"start": v(-177.33, -231.3) * mm, "mid": v(-180.5, -234.48) * mm, "end": v(-177.33, -237.66) * mm});
            skLineSegment(sketch, "E120.MirrorCS", {"start": v(-177.33, -231.3) * mm, "end": v(-158.28, -231.3) * mm});
            skLineSegment(sketch, "E121.MirrorCS", {"start": v(-177.33, -237.66) * mm, "end": v(-158.28, -237.66) * mm});
            skLineSegment(sketch, "E122.MirrorCS", {"start": v(-177.33, -301.16) * mm, "end": v(-158.28, -301.16) * mm});
            skLineSegment(sketch, "E123.MirrorCS", {"start": v(-177.33, -307.5) * mm, "end": v(-158.28, -307.5) * mm});
            skSolve(sketch);
        }
        {
            var Q0;
            Q0=qSketchRegion(id+"F20",true);
            extrude(context, id + "F21", {"entities" : qUnion([Q0]), "operationType" : NewBodyOperationType.REMOVE, "endBound" : BoundingType.THROUGH_ALL, "depth" : 25.4 * mm});
        }
        {
            var Q0;
            Q0=qCreatedBy(makeId("Right.planeOp"),FACE);
            var sketch = newSketch(context, id + "F22", { "sketchPlane" : qUnion([Q0])});
            skLineSegment(sketch, "E124.bottom", {"start": v(165.1, 0) * mm, "end": v(-165.1, 0) * mm});
            skLineSegment(sketch, "E124.top", {"start": v(165.1, 57.15) * mm, "end": v(-165.1, 57.15) * mm});
            skLineSegment(sketch, "E124.left", {"start": v(165.1, 0) * mm, "end": v(165.1, 57.15) * mm});
            skLineSegment(sketch, "E124.right", {"start": v(-165.1, 0) * mm, "end": v(-165.1, 57.15) * mm});
            skSolve(sketch);
        }
        {
            var Q0;
            Q0=makeQuery(id+"F22.imprint","IMPRINT",FACE,{"disambiguationData":[TD([[makeQuery(id+"F22.imprint","IMPRINT",EDGE,{"derivedFrom":sQuery(id+"F22.wireOp",EDGE,"E124.bottom")}),-1.0]])]});
            extrude(context, id + "F23", {"entities" : qUnion([Q0]), "operationType" : NewBodyOperationType.REMOVE, "endBound" : BoundingType.THROUGH_ALL, "depth" : 25.4 * mm, "offsetDistance" : 25.4 * mm});
        }
        {
            var Q0;
            {var subQ0=sQuery(id+"F2.wireOp",EDGE,"E50.0");var subQ1=sQuery(id+"F2.wireOp",EDGE,"E49.0");var subQ2=sQuery(id+"F2.wireOp",EDGE,"E48.0");var subQ3=sQuery(id+"F2.wireOp",EDGE,"E47.0");var subQ4=sQuery(id+"F2.wireOp",EDGE,"E46.0");var subQ5=sQuery(id+"F2.wireOp",EDGE,"E45.0");var subQ6=sQuery(id+"F2.wireOp",EDGE,"E44.0");var subQ7=sQuery(id+"F2.wireOp",EDGE,"E43.0");var subQ8=sQuery(id+"F2.wireOp",EDGE,"E42.0");var subQ9=sQuery(id+"F2.wireOp",EDGE,"E40.0");var subQ10=makeQuery(id+"F3.opExtrude","CAP_FACE",FACE,{"disambiguationData":[OSD([subQ9,subQ8,subQ7,subQ6,subQ5,subQ4,subQ3,subQ2,subQ1,subQ0])],"isStart":true});var subQ11=makeQuery(id+"F6.opExtrude","SWEPT_FACE",FACE,{"disambiguationData":[OSD([sQuery(id+"F5.wireOp",EDGE,"E52.top")])]});Q0=makeQuery(id+"F8.opFillet","BLEND_EDGE",EDGE,{"blendedFrom":[makeQuery(id+"F6.boolean.opBoolean","INTERSECT",EDGE,{"derivedFrom":[subQ10,subQ11]}),makeQuery(id+"F6.boolean.opBoolean","SPLIT",FACE,{"disambiguationData":[TD([subQ11])],"derivedFrom":makeQuery(id+"F4.opShell","OFFSET_FACE",FACE,{"disambiguationData":[OSD([subQ7])]})})],"blendedInto":[makeQuery(id+"F6.boolean.opBoolean","SPLIT",FACE,{"disambiguationData":[TD([subQ11])],"derivedFrom":makeQuery(id+"F4.opShell","OFFSET_FACE",FACE,{"disambiguationData":[OSD([subQ7])]})})]});}
            var Q1;
            Q1=makeQuery(id+"F23.boolean.opBoolean","INTERSECT",EDGE,{"derivedFrom":[makeQuery(id+"F3.opExtrude","CAP_FACE",FACE,{"disambiguationData":[OSD([sQuery(id+"F2.wireOp",EDGE,"E40.0"),sQuery(id+"F2.wireOp",EDGE,"E42.0"),sQuery(id+"F2.wireOp",EDGE,"E43.0"),sQuery(id+"F2.wireOp",EDGE,"E44.0"),sQuery(id+"F2.wireOp",EDGE,"E45.0"),sQuery(id+"F2.wireOp",EDGE,"E46.0"),sQuery(id+"F2.wireOp",EDGE,"E47.0"),sQuery(id+"F2.wireOp",EDGE,"E48.0"),sQuery(id+"F2.wireOp",EDGE,"E49.0"),sQuery(id+"F2.wireOp",EDGE,"E50.0")])],"isStart":true}),makeQuery(id+"F23.opExtrude","SWEPT_FACE",FACE,{"disambiguationData":[OSD([sQuery(id+"F22.wireOp",EDGE,"E124.right")])]})]});
            var Q2;
            Q2=makeQuery(id+"F23.boolean.opBoolean","INTERSECT",EDGE,{"derivedFrom":[makeQuery(id+"F3.opExtrude","CAP_FACE",FACE,{"disambiguationData":[OSD([sQuery(id+"F2.wireOp",EDGE,"E40.0"),sQuery(id+"F2.wireOp",EDGE,"E42.0"),sQuery(id+"F2.wireOp",EDGE,"E43.0"),sQuery(id+"F2.wireOp",EDGE,"E44.0"),sQuery(id+"F2.wireOp",EDGE,"E45.0"),sQuery(id+"F2.wireOp",EDGE,"E46.0"),sQuery(id+"F2.wireOp",EDGE,"E47.0"),sQuery(id+"F2.wireOp",EDGE,"E48.0"),sQuery(id+"F2.wireOp",EDGE,"E49.0"),sQuery(id+"F2.wireOp",EDGE,"E50.0")])],"isStart":true}),makeQuery(id+"F23.opExtrude","SWEPT_FACE",FACE,{"disambiguationData":[OSD([sQuery(id+"F22.wireOp",EDGE,"E124.left")])]})]});
            fillet(context, id + "F24", {"entities" : qUnion([Q0, Q1, Q2]), "radius" : 12.7 * mm, "tangentPropagation" : true, "allowEdgeOverflow" : false});
        }
        {
            var Q0;
            Q0=qCreatedBy(makeId("Right.planeOp"),FACE);
            var sketch = newSketch(context, id + "F25", { "sketchPlane" : qUnion([Q0])});
            skLineSegment(sketch, "E125", {"start": v(114.3, 252.48) * mm, "end": v(160.34, 252.48) * mm});
            skLineSegment(sketch, "E126", {"start": v(165.1, 247.71) * mm, "end": v(165.1, 201.68) * mm});
            skLineSegment(sketch, "E127", {"start": v(165.1, 201.68) * mm, "end": v(163.58, 201.68) * mm});
            skLineSegment(sketch, "E128", {"start": v(163.58, 201.68) * mm, "end": v(163.58, 247.78) * mm});
            skLineSegment(sketch, "E129", {"start": v(160.4, 250.95) * mm, "end": v(114.3, 250.95) * mm});
            skLineSegment(sketch, "E130", {"start": v(114.3, 250.95) * mm, "end": v(114.3, 252.48) * mm});
            skPoint(sketch, "E131.visualSharp", {"position": v(163.58, 250.95) * mm});
            skArc(sketch, "E131.filletArc", {"start": v(163.58, 247.78) * mm, "mid": v(162.65, 250.02) * mm, "end": v(160.4, 250.95) * mm});
            skPoint(sketch, "E132.visualSharp", {"position": v(165.1, 252.48) * mm});
            skArc(sketch, "E132.filletArc", {"start": v(165.1, 247.71) * mm, "mid": v(163.7, 251.08) * mm, "end": v(160.34, 252.48) * mm});
            skSolve(sketch);
        }
        {
            var Q0;
            Q0=qSketchRegion(id+"F25",true);
            extrude(context, id + "F26", {"entities" : qUnion([Q0]), "depth" : 419.1 * mm, "offsetDistance" : 25.4 * mm, "hasSecondDirection" : true, "secondDirectionOppositeDirection" : true, "secondDirectionDepth" : 88.9 * mm});
        }
        {
            var Q0;
            Q0=makeQuery(id+"F19.opExtrude","CAP_FACE",FACE,{"disambiguationData":[OSD([sQuery(id+"F2.wireOp",EDGE,"E40.0"),sQuery(id+"F2.wireOp",EDGE,"E42.0"),sQuery(id+"F2.wireOp",EDGE,"E43.0"),sQuery(id+"F2.wireOp",EDGE,"E44.0"),sQuery(id+"F2.wireOp",EDGE,"E45.0"),sQuery(id+"F2.wireOp",EDGE,"E46.0"),sQuery(id+"F2.wireOp",EDGE,"E47.0"),sQuery(id+"F2.wireOp",EDGE,"E48.0"),sQuery(id+"F2.wireOp",EDGE,"E49.0"),sQuery(id+"F2.wireOp",EDGE,"E50.0")])],"isStart":false});
            var sketch = newSketch(context, id + "F27", { "sketchPlane" : qUnion([Q0])});
            skLineSegment(sketch, "E133.bottom", {"start": v(-155.1, 301.16) * mm, "end": v(-180.5, 301.16) * mm});
            skLineSegment(sketch, "E133.top", {"start": v(-155.1, 237.66) * mm, "end": v(-180.5, 237.66) * mm});
            skLineSegment(sketch, "E133.left", {"start": v(-155.1, 301.16) * mm, "end": v(-155.1, 237.66) * mm});
            skLineSegment(sketch, "E133.right", {"start": v(-180.5, 301.16) * mm, "end": v(-180.5, 237.66) * mm});
            skSolve(sketch);
        }
        {
            var Q0;
            Q0=qSketchRegion(id+"F27",true);
            extrude(context, id + "F28", {"entities" : qUnion([Q0]), "depth" : 4.76 * mm, "offsetDistance" : 25.4 * mm});
        }
        {
            var Q0;
            Q0=makeQuery(id+"F28.opExtrude","SWEPT_FACE",FACE,{"disambiguationData":[OSD([sQuery(id+"F27.wireOp",EDGE,"E133.right")])]});
            var sketch = newSketch(context, id + "F29", { "sketchPlane" : qUnion([Q0])});
            skArc(sketch, "E134", {"start": v(-237.66, 274.64) * mm, "mid": v(-269.4, 279.73) * mm, "end": v(-301.16, 274.64) * mm});
            skSolve(sketch);
        }
        {
            var Q0;
            Q0=makeQuery(id+"F29.imprint","IMPRINT",FACE,{"disambiguationData":[TD([[makeQuery(id+"F29.imprint","IMPRINT",EDGE,{"derivedFrom":sQuery(id+"F29.wireOp",EDGE,"E134")}),1.0]])]});
            var Q1;
            Q1=makeQuery(id+"F28.opExtrude","SWEPT_FACE",FACE,{"disambiguationData":[OSD([sQuery(id+"F27.wireOp",EDGE,"E133.left")])]});
            extrude(context, id + "F30", {"entities" : qUnion([Q0]), "operationType" : NewBodyOperationType.ADD, "endBound" : BoundingType.UP_TO_SURFACE, "oppositeDirection" : true, "depth" : 25.4 * mm, "endBoundEntityFace" : qUnion([Q1]), "offsetDistance" : 25.4 * mm});
        }
        {
            var Q0;
            {var subQ0=sQuery(id+"F27.wireOp",EDGE,"E133.bottom");Q0=makeQuery(id+"F30.boolean.opBoolean","MERGE",EDGE,{"derivedFrom":[makeQuery(id+"F28.opExtrude","CAP_EDGE",EDGE,{"disambiguationData":[OSD([subQ0])],"isStart":false}),makeQuery(id+"F30.opExtrude","SWEPT_EDGE",EDGE,{"disambiguationData":[OSD([subQ0,sQuery(id+"F27.wireOp",EDGE,"E133.right"),sQuery(id+"F29.wireOp",EDGE,"E134")])]})]});}
            var Q1;
            {var subQ0=sQuery(id+"F27.wireOp",EDGE,"E133.top");Q1=makeQuery(id+"F30.boolean.opBoolean","MERGE",EDGE,{"derivedFrom":[makeQuery(id+"F28.opExtrude","CAP_EDGE",EDGE,{"disambiguationData":[OSD([subQ0])],"isStart":false}),makeQuery(id+"F30.opExtrude","SWEPT_EDGE",EDGE,{"disambiguationData":[OSD([subQ0,sQuery(id+"F27.wireOp",EDGE,"E133.right"),sQuery(id+"F29.wireOp",EDGE,"E134")])]})]});}
            fillet(context, id + "F31", {"entities" : qUnion([Q0, Q1]), "radius" : 4.76 * mm, "tangentPropagation" : true, "allowEdgeOverflow" : false});
        }
        {
            var Q0;
            Q0=makeQuery(id+"F28.opExtrude","CAP_FACE",FACE,{"disambiguationData":[OSD([sQuery(id+"F27.wireOp",EDGE,"E133.bottom"),sQuery(id+"F27.wireOp",EDGE,"E133.top"),sQuery(id+"F27.wireOp",EDGE,"E133.left"),sQuery(id+"F27.wireOp",EDGE,"E133.right")])],"isStart":true});
            var sketch = newSketch(context, id + "F32", { "sketchPlane" : qUnion([Q0])});
            skCircle(sketch, "E135", {"center": v(-178.92, -301.16) * mm, "radius": 1.59 * mm});
            skCircle(sketch, "E136", {"center": v(-156.7, -301.16) * mm, "radius": 1.59 * mm});
            skSolve(sketch);
        }
        {
            var Q0;
            Q0=qSketchRegion(id+"F32",true);
            var Q1;
            Q1=makeQuery(id+"F28.opExtrude","SWEPT_EDGE",EDGE,{"disambiguationData":[OSD([sQuery(id+"F27.wireOp",EDGE,"E133.bottom"),sQuery(id+"F27.wireOp",EDGE,"E133.right")])]});
            var Q2;
            {var subQ0=sQuery(id+"F29.wireOp",EDGE,"E134");var subQ1=sQuery(id+"F27.wireOp",EDGE,"E133.right");var subQ2=sQuery(id+"F27.wireOp",EDGE,"E133.bottom");Q2=makeQuery(id+"F31.opFillet","BLEND_EDGE",EDGE,{"blendedFrom":[makeQuery(id+"F30.boolean.opBoolean","MERGE",EDGE,{"derivedFrom":[makeQuery(id+"F28.opExtrude","CAP_EDGE",EDGE,{"disambiguationData":[OSD([subQ2])],"isStart":false}),makeQuery(id+"F30.opExtrude","SWEPT_EDGE",EDGE,{"disambiguationData":[OSD([subQ2,subQ1,subQ0])]})]}),makeQuery(id+"F30.boolean.opBoolean","MERGE",FACE,{"derivedFrom":[makeQuery(id+"F28.opExtrude","SWEPT_FACE",FACE,{"disambiguationData":[OSD([subQ1])]}),makeQuery(id+"F30.opExtrude","CAP_FACE",FACE,{"disambiguationData":[OSD([subQ1,subQ0])],"isStart":true})]})],"blendedInto":[makeQuery(id+"F30.boolean.opBoolean","MERGE",FACE,{"derivedFrom":[makeQuery(id+"F28.opExtrude","SWEPT_FACE",FACE,{"disambiguationData":[OSD([subQ1])]}),makeQuery(id+"F30.opExtrude","CAP_FACE",FACE,{"disambiguationData":[OSD([subQ1,subQ0])],"isStart":true})]})]});}
            var Q3;
            Q3=makeQuery(id+"F30.opExtrude","CAP_EDGE",EDGE,{"disambiguationData":[OSD([sQuery(id+"F29.wireOp",EDGE,"E134")])],"isStart":true});
            var Q4;
            {var subQ0=sQuery(id+"F29.wireOp",EDGE,"E134");var subQ1=sQuery(id+"F27.wireOp",EDGE,"E133.right");var subQ2=sQuery(id+"F27.wireOp",EDGE,"E133.top");Q4=makeQuery(id+"F31.opFillet","BLEND_EDGE",EDGE,{"blendedFrom":[makeQuery(id+"F30.boolean.opBoolean","MERGE",EDGE,{"derivedFrom":[makeQuery(id+"F28.opExtrude","CAP_EDGE",EDGE,{"disambiguationData":[OSD([subQ2])],"isStart":false}),makeQuery(id+"F30.opExtrude","SWEPT_EDGE",EDGE,{"disambiguationData":[OSD([subQ2,subQ1,subQ0])]})]}),makeQuery(id+"F30.boolean.opBoolean","MERGE",FACE,{"derivedFrom":[makeQuery(id+"F28.opExtrude","SWEPT_FACE",FACE,{"disambiguationData":[OSD([subQ1])]}),makeQuery(id+"F30.opExtrude","CAP_FACE",FACE,{"disambiguationData":[OSD([subQ1,subQ0])],"isStart":true})]})],"blendedInto":[makeQuery(id+"F30.boolean.opBoolean","MERGE",FACE,{"derivedFrom":[makeQuery(id+"F28.opExtrude","SWEPT_FACE",FACE,{"disambiguationData":[OSD([subQ1])]}),makeQuery(id+"F30.opExtrude","CAP_FACE",FACE,{"disambiguationData":[OSD([subQ1,subQ0])],"isStart":true})]})]});}
            var Q5;
            Q5=makeQuery(id+"F28.opExtrude","SWEPT_EDGE",EDGE,{"disambiguationData":[OSD([sQuery(id+"F27.wireOp",EDGE,"E133.top"),sQuery(id+"F27.wireOp",EDGE,"E133.right")])]});
            sweep(context, id + "F33", {"operationType" : NewBodyOperationType.ADD, "profiles" : qUnion([Q0]), "path" : qUnion([Q1, Q2, Q3, Q4, Q5])});
        }
        {
            var Q0;
            Q0=makeQuery(id+"F26.opExtrude","SWEPT_FACE",FACE,{"disambiguationData":[OSD([sQuery(id+"F25.wireOp",EDGE,"E126")])]});
            var sketch = newSketch(context, id + "F34", { "sketchPlane" : qUnion([Q0])});
            skLineSegment(sketch, "E137.bottom", {"start": v(-63.5, 201.68) * mm, "end": v(-266.7, 201.68) * mm});
            skLineSegment(sketch, "E137.top", {"start": v(-63.5, 250.95) * mm, "end": v(-266.7, 250.95) * mm});
            skLineSegment(sketch, "E137.left", {"start": v(-63.5, 201.68) * mm, "end": v(-63.5, 250.95) * mm});
            skLineSegment(sketch, "E137.right", {"start": v(-266.7, 201.68) * mm, "end": v(-266.7, 250.95) * mm});
            skCircle(sketch, "E138", {"center": v(76.2, 227.08) * mm, "radius": 3.18 * mm});
            skCircle(sketch, "E139", {"center": v(-50.8, 227.08) * mm, "radius": 3.18 * mm});
            skCircle(sketch, "E140", {"center": v(-279.4, 227.08) * mm, "radius": 3.18 * mm});
            skCircle(sketch, "E141", {"center": v(-406.4, 227.08) * mm, "radius": 3.18 * mm});
            skLineSegment(sketch, "E142", {"start": v(12.7, 75.54) * mm, "end": v(12.7, 140.98) * mm, "construction": true});
            skLineSegment(sketch, "E143", {"start": v(-342.9, 55.46) * mm, "end": v(-342.9, 150.6) * mm, "construction": true});
            skSolve(sketch);
        }
        {
            var Q0;
            Q0=qSketchRegion(id+"F34",true);
            extrude(context, id + "F35", {"entities" : qUnion([Q0]), "operationType" : NewBodyOperationType.REMOVE, "endBound" : BoundingType.THROUGH_ALL, "oppositeDirection" : true, "depth" : 25.4 * mm, "offsetDistance" : 25.4 * mm});
        }
        {
            var Q0;
            Q0=makeQuery(id+"F26.opExtrude","CAP_EDGE",EDGE,{"disambiguationData":[OSD([sQuery(id+"F25.wireOp",EDGE,"E127")])],"isStart":true});
            var Q1;
            Q1=makeQuery(id+"F35.boolean.opBoolean","COPY",EDGE,{"derivedFrom":makeQuery(id+"F35.opExtrude","SWEPT_EDGE",EDGE,{"disambiguationData":[OSD([sQuery(id+"F25.wireOp",EDGE,"E126"),sQuery(id+"F25.wireOp",EDGE,"E127"),sQuery(id+"F34.wireOp",EDGE,"E137.bottom"),sQuery(id+"F34.wireOp",EDGE,"E137.left")])]})});
            var Q2;
            Q2=makeQuery(id+"F35.boolean.opBoolean","COPY",EDGE,{"derivedFrom":makeQuery(id+"F35.opExtrude","SWEPT_EDGE",EDGE,{"disambiguationData":[OSD([sQuery(id+"F25.wireOp",EDGE,"E126"),sQuery(id+"F25.wireOp",EDGE,"E127"),sQuery(id+"F34.wireOp",EDGE,"E137.bottom"),sQuery(id+"F34.wireOp",EDGE,"E137.right")])]})});
            var Q3;
            Q3=makeQuery(id+"F26.opExtrude","CAP_EDGE",EDGE,{"disambiguationData":[OSD([sQuery(id+"F25.wireOp",EDGE,"E127")])],"isStart":false});
            fillet(context, id + "F36", {"entities" : qUnion([Q0, Q1, Q2, Q3]), "radius" : 12.7 * mm, "tangentPropagation" : true, "allowEdgeOverflow" : false});
        }
        {
            var Q0;
            Q0=makeQuery(id+"F18.opExtrude","CAP_EDGE",EDGE,{"disambiguationData":[OSD([sQuery(id+"F17.wireOp",EDGE,"E79.left")])],"isStart":false});
            var Q1;
            Q1=makeQuery(id+"F18.opExtrude","CAP_EDGE",EDGE,{"disambiguationData":[OSD([sQuery(id+"F17.wireOp",EDGE,"E79.right")])],"isStart":false});
            fillet(context, id + "F37", {"entities" : qUnion([Q0, Q1]), "radius" : 10.29 * mm, "tangentPropagation" : true, "allowEdgeOverflow" : false});
        }
        {
            var Q0;
            Q0=makeQuery(id+"F18.opExtrude","CAP_EDGE",EDGE,{"disambiguationData":[OSD([sQuery(id+"F17.wireOp",EDGE,"E79.bottom")])],"isStart":true});
            fillet(context, id + "F38", {"entities" : qUnion([Q0]), "radius" : 50.8 * mm, "tangentPropagation" : true, "allowEdgeOverflow" : false});
        }
        {
            var Q0;
            Q0=makeQuery(id+"F18.opExtrude","SWEPT_FACE",FACE,{"disambiguationData":[OSD([sQuery(id+"F17.wireOp",EDGE,"E79.bottom")])]});
            var Q1;
            Q1=makeQuery(id+"F38.opFillet","BLEND_FACE",FACE,{"disambiguationData":[OSD([sQuery(id+"F17.wireOp",EDGE,"E79.bottom")])]});
            var Q2;
            Q2=makeQuery(id+"F18.opExtrude","CAP_FACE",FACE,{"disambiguationData":[OSD([sQuery(id+"F17.wireOp",EDGE,"E79.bottom"),sQuery(id+"F17.wireOp",EDGE,"E79.top"),sQuery(id+"F17.wireOp",EDGE,"E79.left"),sQuery(id+"F17.wireOp",EDGE,"E79.right")])],"isStart":true});
            var Q3;
            Q3=makeQuery(id+"F18.opExtrude","SWEPT_FACE",FACE,{"disambiguationData":[OSD([sQuery(id+"F17.wireOp",EDGE,"E79.top")])]});
            shell(context, id + "F39", {"entities" : qUnion([Q0, Q1, Q2, Q3]), "thickness" : 1.52 * mm});
        }
        {
            var Q0;
            Q0=qCreatedBy(makeId("Front.planeOp"),FACE);
            var sketch = newSketch(context, id + "F40", { "sketchPlane" : qUnion([Q0])});
            skCircle(sketch, "E144", {"center": v(-69.85, 533.4) * mm, "radius": 14.29 * mm});
            skSolve(sketch);
        }
        {
            var Q0;
            Q0=qSketchRegion(id+"F40",true);
            extrude(context, id + "F41", {"entities" : qUnion([Q0]), "operationType" : NewBodyOperationType.REMOVE, "endBound" : BoundingType.THROUGH_ALL, "oppositeDirection" : true, "depth" : 25.4 * mm, "offsetDistance" : 25.4 * mm, "hasSecondDirection" : true, "secondDirectionBound" : SecondDirectionBoundingType.THROUGH_ALL, "secondDirectionOppositeDirection" : false, "secondDirectionDepth" : 25.4 * mm});
        }
    });
